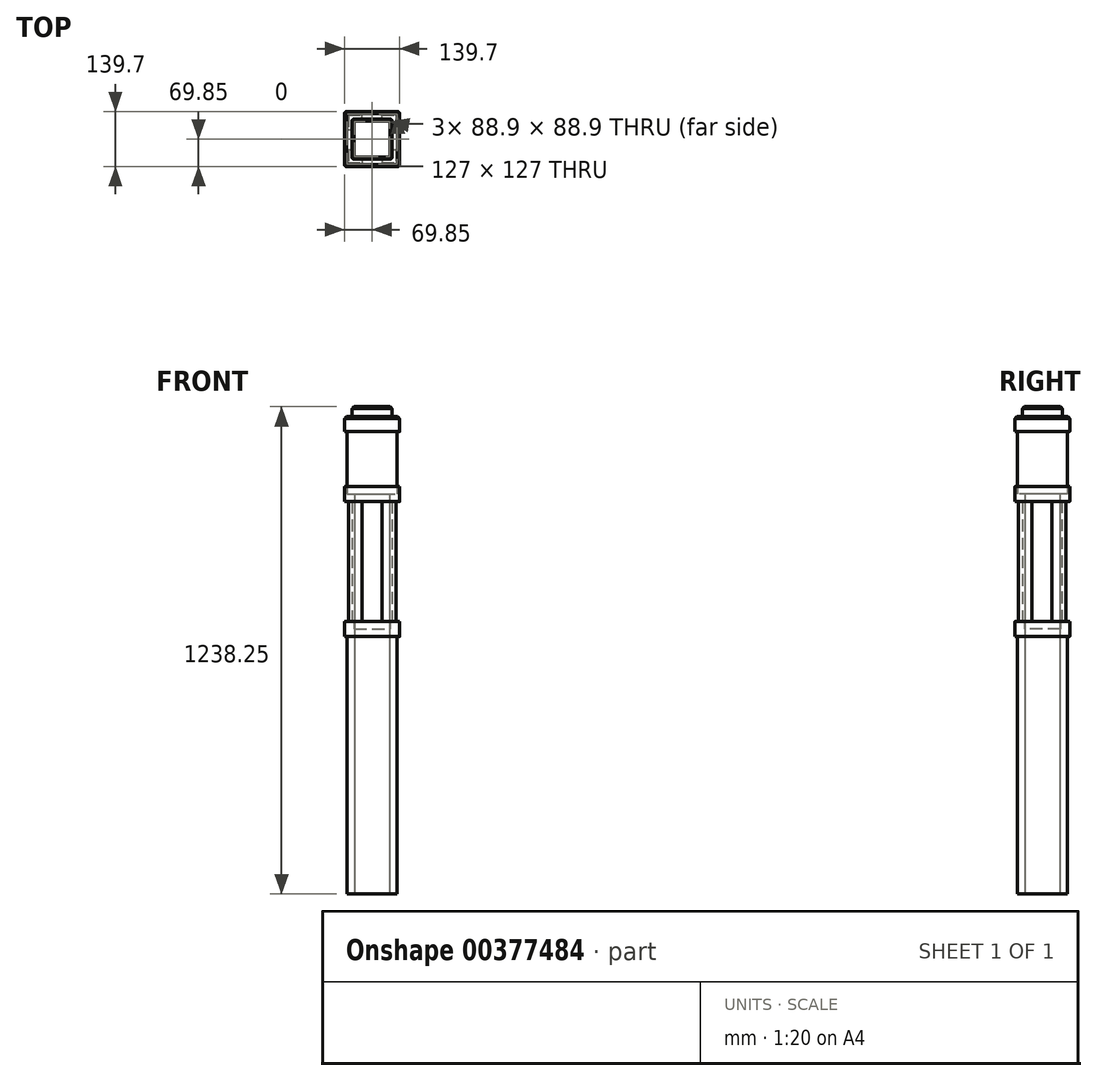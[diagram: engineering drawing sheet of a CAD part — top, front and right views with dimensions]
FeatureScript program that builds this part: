
annotation { "Feature Type Name" : "Feature", "Feature Type Description" : "" }
export const myFeature = defineFeature(function(context is Context, id is Id, definition is map)
    precondition{}
    {
        {
            var Q0;
            Q0=qCreatedBy(makeId("Top.planeOp"),FACE);
            var sketch = newSketch(context, id + "F0", { "sketchPlane" : qUnion([Q0])});
            skLineSegment(sketch, "E0.bottom", {"start": v(-44.45, 44.45) * mm, "end": v(44.45, 44.45) * mm});
            skLineSegment(sketch, "E0.top", {"start": v(-44.45, -44.45) * mm, "end": v(44.45, -44.45) * mm});
            skLineSegment(sketch, "E0.left", {"start": v(-44.45, 44.45) * mm, "end": v(-44.45, -44.45) * mm});
            skLineSegment(sketch, "E0.right", {"start": v(44.45, 44.45) * mm, "end": v(44.45, -44.45) * mm});
            skPoint(sketch, "E0.middle", {"position": v(0, 0) * mm});
            skSolve(sketch);
        }
        {
            var Q0;
            Q0 = qSketchRegion(id + "F0", true);
            extrude(context, id + "F1", {"entities" : qUnion([Q0]), "depth" : 1193.8 * mm, "offsetDistance" : 25.4 * mm});
        }
        {
            var Q0;
            Q0=makeQuery(id+"F1.opExtrude","CAP_FACE",FACE,{"disambiguationData":[OSD([sQuery(id+"F0.wireOp",EDGE,"E0.bottom"),sQuery(id+"F0.wireOp",EDGE,"E0.top"),sQuery(id+"F0.wireOp",EDGE,"E0.left"),sQuery(id+"F0.wireOp",EDGE,"E0.right")])],"isStart":true});
            var sketch = newSketch(context, id + "F2", { "sketchPlane" : qUnion([Q0])});
            skLineSegment(sketch, "E1.bottom", {"start": v(-63.5, 63.5) * mm, "end": v(63.5, 63.5) * mm});
            skLineSegment(sketch, "E1.top", {"start": v(-63.5, -63.5) * mm, "end": v(63.5, -63.5) * mm});
            skLineSegment(sketch, "E1.left", {"start": v(-63.5, 63.5) * mm, "end": v(-63.5, -63.5) * mm});
            skLineSegment(sketch, "E1.right", {"start": v(63.5, 63.5) * mm, "end": v(63.5, -63.5) * mm});
            skPoint(sketch, "E1.middle", {"position": v(0, 0) * mm});
            skLineSegment(sketch, "E2.bottom", {"start": v(-44.45, 44.45) * mm, "end": v(44.45, 44.45) * mm});
            skLineSegment(sketch, "E2.top", {"start": v(-44.45, -44.45) * mm, "end": v(44.45, -44.45) * mm});
            skLineSegment(sketch, "E2.left", {"start": v(-44.45, 44.45) * mm, "end": v(-44.45, -44.45) * mm});
            skLineSegment(sketch, "E2.right", {"start": v(44.45, 44.45) * mm, "end": v(44.45, -44.45) * mm});
            skLineSegment(sketch, "E3", {"start": v(44.45, 44.45) * mm, "end": v(63.5, 63.5) * mm});
            skLineSegment(sketch, "E4", {"start": v(44.45, -44.45) * mm, "end": v(63.5, -63.5) * mm});
            skLineSegment(sketch, "E5", {"start": v(-44.45, -44.45) * mm, "end": v(-63.5, -63.5) * mm});
            skLineSegment(sketch, "E6", {"start": v(-44.45, 44.45) * mm, "end": v(-63.5, 63.5) * mm});
            skSolve(sketch);
        }
        {
            var Q0;
            Q0 = qSketchRegion(id + "F2", true);
            extrude(context, id + "F3", {"entities" : qUnion([Q0]), "oppositeDirection" : true, "depth" : 673.1 * mm, "offsetDistance" : 25.4 * mm});
        }
        {
            var Q0;
            Q0=makeQuery(id+"F3.opExtrude","CAP_FACE",FACE,{"disambiguationData":[OSD([sQuery(id+"F2.wireOp",EDGE,"E1.bottom"),sQuery(id+"F2.wireOp",EDGE,"E1.top"),sQuery(id+"F2.wireOp",EDGE,"E1.left"),sQuery(id+"F2.wireOp",EDGE,"E1.right"),sQuery(id+"F2.wireOp",EDGE,"E2.bottom"),sQuery(id+"F2.wireOp",EDGE,"E2.top"),sQuery(id+"F2.wireOp",EDGE,"E2.left"),sQuery(id+"F2.wireOp",EDGE,"E2.right")])],"isStart":false});
            var sketch = newSketch(context, id + "F4", { "sketchPlane" : qUnion([Q0])});
            skLineSegment(sketch, "E7.bottom", {"start": v(-69.85, 69.85) * mm, "end": v(69.85, 69.85) * mm});
            skLineSegment(sketch, "E7.top", {"start": v(-69.85, -69.85) * mm, "end": v(69.85, -69.85) * mm});
            skLineSegment(sketch, "E7.left", {"start": v(-69.85, 69.85) * mm, "end": v(-69.85, -69.85) * mm});
            skLineSegment(sketch, "E7.right", {"start": v(69.85, 69.85) * mm, "end": v(69.85, -69.85) * mm});
            skPoint(sketch, "E7.middle", {"position": v(0, 0) * mm});
            skLineSegment(sketch, "E8.bottom", {"start": v(-63.5, 63.5) * mm, "end": v(63.5, 63.5) * mm});
            skLineSegment(sketch, "E8.top", {"start": v(-63.5, -63.5) * mm, "end": v(63.5, -63.5) * mm});
            skLineSegment(sketch, "E8.left", {"start": v(-63.5, 63.5) * mm, "end": v(-63.5, -63.5) * mm});
            skLineSegment(sketch, "E8.right", {"start": v(63.5, 63.5) * mm, "end": v(63.5, -63.5) * mm});
            skSolve(sketch);
        }
        {
            var Q0;
            Q0 = qSketchRegion(id + "F4", true);
            extrude(context, id + "F5", {"entities" : qUnion([Q0]), "oppositeDirection" : true, "depth" : 19.05 * mm, "offsetDistance" : 25.4 * mm});
        }
        {
            var Q0;
            Q0=makeQuery(id+"F5.opExtrude","CAP_FACE",FACE,{"disambiguationData":[OSD([sQuery(id+"F4.wireOp",EDGE,"E7.bottom"),sQuery(id+"F4.wireOp",EDGE,"E7.top"),sQuery(id+"F4.wireOp",EDGE,"E7.left"),sQuery(id+"F4.wireOp",EDGE,"E7.right"),sQuery(id+"F4.wireOp",EDGE,"E8.bottom"),sQuery(id+"F4.wireOp",EDGE,"E8.top"),sQuery(id+"F4.wireOp",EDGE,"E8.left"),sQuery(id+"F4.wireOp",EDGE,"E8.right")])],"isStart":true});
            var sketch = newSketch(context, id + "F6", { "sketchPlane" : qUnion([Q0])});
            skLineSegment(sketch, "E9.bottom", {"start": v(-69.85, 69.85) * mm, "end": v(69.85, 69.85) * mm});
            skLineSegment(sketch, "E9.top", {"start": v(-69.85, -69.85) * mm, "end": v(69.85, -69.85) * mm});
            skLineSegment(sketch, "E9.left", {"start": v(-69.85, 69.85) * mm, "end": v(-69.85, -69.85) * mm});
            skLineSegment(sketch, "E9.right", {"start": v(69.85, 69.85) * mm, "end": v(69.85, -69.85) * mm});
            skPoint(sketch, "E9.middle", {"position": v(0, 0) * mm});
            skLineSegment(sketch, "E10.bottom", {"start": v(-45.72, 45.72) * mm, "end": v(45.72, 45.72) * mm});
            skLineSegment(sketch, "E10.top", {"start": v(-45.72, -45.72) * mm, "end": v(45.72, -45.72) * mm});
            skLineSegment(sketch, "E10.left", {"start": v(-45.72, 45.72) * mm, "end": v(-45.72, -45.72) * mm});
            skLineSegment(sketch, "E10.right", {"start": v(45.72, 45.72) * mm, "end": v(45.72, -45.72) * mm});
            skSolve(sketch);
        }
        {
            var Q0;
            Q0 = qSketchRegion(id + "F6", true);
            extrude(context, id + "F7", {"entities" : qUnion([Q0]), "operationType" : NewBodyOperationType.ADD, "depth" : 19.05 * mm, "offsetDistance" : 25.4 * mm});
        }
        {
            var Q0;
            Q0=makeQuery(id+"F7.opExtrude","CAP_FACE",FACE,{"disambiguationData":[OSD([sQuery(id+"F6.wireOp",EDGE,"E9.bottom"),sQuery(id+"F6.wireOp",EDGE,"E9.top"),sQuery(id+"F6.wireOp",EDGE,"E9.left"),sQuery(id+"F6.wireOp",EDGE,"E9.right"),sQuery(id+"F6.wireOp",EDGE,"E10.bottom"),sQuery(id+"F6.wireOp",EDGE,"E10.top"),sQuery(id+"F6.wireOp",EDGE,"E10.left"),sQuery(id+"F6.wireOp",EDGE,"E10.right")])],"isStart":false});
            var sketch = newSketch(context, id + "F8", { "sketchPlane" : qUnion([Q0])});
            skLineSegment(sketch, "E11.bottom", {"start": v(-50.8, 50.8) * mm, "end": v(50.8, 50.8) * mm});
            skLineSegment(sketch, "E11.top", {"start": v(-50.8, -50.8) * mm, "end": v(50.8, -50.8) * mm});
            skLineSegment(sketch, "E11.left", {"start": v(-50.8, 50.8) * mm, "end": v(-50.8, -50.8) * mm});
            skLineSegment(sketch, "E11.right", {"start": v(50.8, 50.8) * mm, "end": v(50.8, -50.8) * mm});
            skPoint(sketch, "E11.middle", {"position": v(0, 0) * mm});
            skLineSegment(sketch, "E12.bottom", {"start": v(-44.45, 44.45) * mm, "end": v(44.45, 44.45) * mm});
            skLineSegment(sketch, "E12.top", {"start": v(-44.45, -44.45) * mm, "end": v(44.45, -44.45) * mm});
            skLineSegment(sketch, "E12.left", {"start": v(-44.45, 44.45) * mm, "end": v(-44.45, -44.45) * mm});
            skLineSegment(sketch, "E12.right", {"start": v(44.45, 44.45) * mm, "end": v(44.45, -44.45) * mm});
            skSolve(sketch);
        }
        {
            var Q0;
            Q0 = qSketchRegion(id + "F8", true);
            extrude(context, id + "F9", {"entities" : qUnion([Q0]), "depth" : 304.8 * mm, "offsetDistance" : 25.4 * mm});
        }
        {
            var Q0;
            Q0=makeQuery(id+"F9.opExtrude","CAP_FACE",FACE,{"disambiguationData":[OSD([sQuery(id+"F8.wireOp",EDGE,"E11.bottom"),sQuery(id+"F8.wireOp",EDGE,"E11.top"),sQuery(id+"F8.wireOp",EDGE,"E11.left"),sQuery(id+"F8.wireOp",EDGE,"E11.right"),sQuery(id+"F8.wireOp",EDGE,"E12.bottom"),sQuery(id+"F8.wireOp",EDGE,"E12.top"),sQuery(id+"F8.wireOp",EDGE,"E12.left"),sQuery(id+"F8.wireOp",EDGE,"E12.right")])],"isStart":false});
            var sketch = newSketch(context, id + "F10", { "sketchPlane" : qUnion([Q0])});
            skLineSegment(sketch, "E13.bottom", {"start": v(-69.85, 69.85) * mm, "end": v(69.85, 69.85) * mm});
            skLineSegment(sketch, "E13.top", {"start": v(-69.85, -69.85) * mm, "end": v(69.85, -69.85) * mm});
            skLineSegment(sketch, "E13.left", {"start": v(-69.85, 69.85) * mm, "end": v(-69.85, -69.85) * mm});
            skLineSegment(sketch, "E13.right", {"start": v(69.85, 69.85) * mm, "end": v(69.85, -69.85) * mm});
            skPoint(sketch, "E13.middle", {"position": v(0, 0) * mm});
            skLineSegment(sketch, "E14.bottom", {"start": v(-44.45, 44.45) * mm, "end": v(44.45, 44.45) * mm});
            skLineSegment(sketch, "E14.top", {"start": v(-44.45, -44.45) * mm, "end": v(44.45, -44.45) * mm});
            skLineSegment(sketch, "E14.left", {"start": v(-44.45, 44.45) * mm, "end": v(-44.45, -44.45) * mm});
            skLineSegment(sketch, "E14.right", {"start": v(44.45, 44.45) * mm, "end": v(44.45, -44.45) * mm});
            skSolve(sketch);
        }
        {
            var Q0;
            Q0 = qSketchRegion(id + "F10", true);
            extrude(context, id + "F11", {"entities" : qUnion([Q0]), "depth" : 19.05 * mm, "offsetDistance" : 25.4 * mm});
        }
        {
            var Q0;
            Q0=makeQuery(id+"F11.opExtrude","CAP_FACE",FACE,{"disambiguationData":[OSD([sQuery(id+"F10.wireOp",EDGE,"E13.bottom"),sQuery(id+"F10.wireOp",EDGE,"E13.top"),sQuery(id+"F10.wireOp",EDGE,"E13.left"),sQuery(id+"F10.wireOp",EDGE,"E13.right"),sQuery(id+"F10.wireOp",EDGE,"E14.bottom"),sQuery(id+"F10.wireOp",EDGE,"E14.top"),sQuery(id+"F10.wireOp",EDGE,"E14.left"),sQuery(id+"F10.wireOp",EDGE,"E14.right")])],"isStart":false});
            var sketch = newSketch(context, id + "F12", { "sketchPlane" : qUnion([Q0])});
            skLineSegment(sketch, "E15.bottom", {"start": v(-69.85, 69.85) * mm, "end": v(69.85, 69.85) * mm});
            skLineSegment(sketch, "E15.top", {"start": v(-69.85, -69.85) * mm, "end": v(69.85, -69.85) * mm});
            skLineSegment(sketch, "E15.left", {"start": v(-69.85, 69.85) * mm, "end": v(-69.85, -69.85) * mm});
            skLineSegment(sketch, "E15.right", {"start": v(69.85, 69.85) * mm, "end": v(69.85, -69.85) * mm});
            skPoint(sketch, "E15.middle", {"position": v(0, 0) * mm});
            skLineSegment(sketch, "E16.bottom", {"start": v(-63.5, 63.5) * mm, "end": v(63.5, 63.5) * mm});
            skLineSegment(sketch, "E16.top", {"start": v(-63.5, -63.5) * mm, "end": v(63.5, -63.5) * mm});
            skLineSegment(sketch, "E16.left", {"start": v(-63.5, 63.5) * mm, "end": v(-63.5, -63.5) * mm});
            skLineSegment(sketch, "E16.right", {"start": v(63.5, 63.5) * mm, "end": v(63.5, -63.5) * mm});
            skSolve(sketch);
        }
        {
            var Q0;
            Q0 = qSketchRegion(id + "F12", true);
            extrude(context, id + "F13", {"entities" : qUnion([Q0]), "operationType" : NewBodyOperationType.ADD, "depth" : 19.05 * mm, "offsetDistance" : 25.4 * mm});
        }
        {
            var Q0;
            Q0=makeQuery(id+"F11.opExtrude","CAP_FACE",FACE,{"disambiguationData":[OSD([sQuery(id+"F10.wireOp",EDGE,"E13.bottom"),sQuery(id+"F10.wireOp",EDGE,"E13.top"),sQuery(id+"F10.wireOp",EDGE,"E13.left"),sQuery(id+"F10.wireOp",EDGE,"E13.right"),sQuery(id+"F10.wireOp",EDGE,"E14.bottom"),sQuery(id+"F10.wireOp",EDGE,"E14.top"),sQuery(id+"F10.wireOp",EDGE,"E14.left"),sQuery(id+"F10.wireOp",EDGE,"E14.right")])],"isStart":false});
            var sketch = newSketch(context, id + "F14", { "sketchPlane" : qUnion([Q0])});
            skLineSegment(sketch, "E17.bottom", {"start": v(-63.5, 63.5) * mm, "end": v(63.5, 63.5) * mm});
            skLineSegment(sketch, "E17.top", {"start": v(-63.5, -63.5) * mm, "end": v(63.5, -63.5) * mm});
            skLineSegment(sketch, "E17.left", {"start": v(-63.5, 63.5) * mm, "end": v(-63.5, -63.5) * mm});
            skLineSegment(sketch, "E17.right", {"start": v(63.5, 63.5) * mm, "end": v(63.5, -63.5) * mm});
            skPoint(sketch, "E17.middle", {"position": v(0, 0) * mm});
            skLineSegment(sketch, "E18.bottom", {"start": v(-44.45, 44.45) * mm, "end": v(44.45, 44.45) * mm});
            skLineSegment(sketch, "E18.top", {"start": v(-44.45, -44.45) * mm, "end": v(44.45, -44.45) * mm});
            skLineSegment(sketch, "E18.left", {"start": v(-44.45, 44.45) * mm, "end": v(-44.45, -44.45) * mm});
            skLineSegment(sketch, "E18.right", {"start": v(44.45, 44.45) * mm, "end": v(44.45, -44.45) * mm});
            skSolve(sketch);
        }
        {
            var Q0;
            Q0 = qSketchRegion(id + "F14", true);
            extrude(context, id + "F15", {"entities" : qUnion([Q0]), "depth" : 177.8 * mm, "offsetDistance" : 25.4 * mm});
        }
        {
            var Q0;
            Q0=makeQuery(id+"F7.opExtrude","CAP_FACE",FACE,{"disambiguationData":[OSD([sQuery(id+"F6.wireOp",EDGE,"E9.bottom"),sQuery(id+"F6.wireOp",EDGE,"E9.top"),sQuery(id+"F6.wireOp",EDGE,"E9.left"),sQuery(id+"F6.wireOp",EDGE,"E9.right"),sQuery(id+"F6.wireOp",EDGE,"E10.bottom"),sQuery(id+"F6.wireOp",EDGE,"E10.top"),sQuery(id+"F6.wireOp",EDGE,"E10.left"),sQuery(id+"F6.wireOp",EDGE,"E10.right")])],"isStart":false});
            var sketch = newSketch(context, id + "F16", { "sketchPlane" : qUnion([Q0])});
            skLineSegment(sketch, "E19.bottom", {"start": v(-60.32, 60.33) * mm, "end": v(60.33, 60.33) * mm});
            skLineSegment(sketch, "E19.top", {"start": v(-60.33, -60.33) * mm, "end": v(60.32, -60.33) * mm});
            skLineSegment(sketch, "E19.left", {"start": v(-60.32, 60.33) * mm, "end": v(-60.33, -60.33) * mm});
            skLineSegment(sketch, "E19.right", {"start": v(60.33, 60.33) * mm, "end": v(60.32, -60.33) * mm});
            skPoint(sketch, "E19.middle", {"position": v(0, 0) * mm});
            skLineSegment(sketch, "E20.bottom", {"start": v(-50.8, -50.8) * mm, "end": v(50.8, -50.8) * mm});
            skLineSegment(sketch, "E20.top", {"start": v(-50.8, 50.8) * mm, "end": v(50.8, 50.8) * mm});
            skLineSegment(sketch, "E20.left", {"start": v(-50.8, -50.8) * mm, "end": v(-50.8, 50.8) * mm});
            skLineSegment(sketch, "E20.right", {"start": v(50.8, -50.8) * mm, "end": v(50.8, 50.8) * mm});
            skSolve(sketch);
        }
        {
            var Q0;
            Q0 = qSketchRegion(id + "F16", true);
            extrude(context, id + "F17", {"entities" : qUnion([Q0]), "depth" : 304.8 * mm, "offsetDistance" : 25.4 * mm});
        }
        {
            var Q0;
            Q0=makeQuery(id+"F17.opExtrude","CAP_FACE",FACE,{"disambiguationData":[OSD([sQuery(id+"F16.wireOp",EDGE,"E19.bottom"),sQuery(id+"F16.wireOp",EDGE,"E19.top"),sQuery(id+"F16.wireOp",EDGE,"E19.left"),sQuery(id+"F16.wireOp",EDGE,"E19.right"),sQuery(id+"F16.wireOp",EDGE,"E20.bottom"),sQuery(id+"F16.wireOp",EDGE,"E20.top"),sQuery(id+"F16.wireOp",EDGE,"E20.left"),sQuery(id+"F16.wireOp",EDGE,"E20.right")])],"isStart":false});
            var sketch = newSketch(context, id + "F18", { "sketchPlane" : qUnion([Q0])});
            skLineSegment(sketch, "E21.bottom", {"start": v(-60.32, 24.53) * mm, "end": v(-50.8, 24.53) * mm});
            skLineSegment(sketch, "E21.top", {"start": v(-60.32, -26.27) * mm, "end": v(-50.8, -26.27) * mm});
            skLineSegment(sketch, "E21.left", {"start": v(-60.32, 24.53) * mm, "end": v(-60.32, -26.27) * mm});
            skLineSegment(sketch, "E21.right", {"start": v(-50.8, 24.53) * mm, "end": v(-50.8, -26.27) * mm});
            skLineSegment(sketch, "E22.bottom", {"start": v(50.8, 24.53) * mm, "end": v(60.33, 24.53) * mm});
            skLineSegment(sketch, "E22.top", {"start": v(50.8, -26.27) * mm, "end": v(60.32, -26.27) * mm});
            skLineSegment(sketch, "E22.left", {"start": v(50.8, 24.53) * mm, "end": v(50.8, -26.27) * mm});
            skLineSegment(sketch, "E22.right", {"start": v(60.32, 24.53) * mm, "end": v(60.32, -26.27) * mm});
            skLineSegment(sketch, "E23.bottom", {"start": v(-25.4, 50.8) * mm, "end": v(25.4, 50.8) * mm});
            skLineSegment(sketch, "E23.top", {"start": v(-25.4, 60.33) * mm, "end": v(25.4, 60.33) * mm});
            skLineSegment(sketch, "E23.left", {"start": v(-25.4, 50.8) * mm, "end": v(-25.4, 60.33) * mm});
            skLineSegment(sketch, "E23.right", {"start": v(25.4, 50.8) * mm, "end": v(25.4, 60.33) * mm});
            skLineSegment(sketch, "E24.bottom", {"start": v(25.4, -50.8) * mm, "end": v(-25.4, -50.8) * mm});
            skLineSegment(sketch, "E24.top", {"start": v(25.4, -60.33) * mm, "end": v(-25.4, -60.33) * mm});
            skLineSegment(sketch, "E24.left", {"start": v(25.4, -50.8) * mm, "end": v(25.4, -60.33) * mm});
            skLineSegment(sketch, "E24.right", {"start": v(-25.4, -50.8) * mm, "end": v(-25.4, -60.33) * mm});
            skSolve(sketch);
        }
        {
            var Q0;
            Q0 = qSketchRegion(id + "F18", true);
            extrude(context, id + "F19", {"entities" : qUnion([Q0]), "operationType" : NewBodyOperationType.REMOVE, "oppositeDirection" : true, "depth" : 304.8 * mm, "offsetDistance" : 25.4 * mm});
        }
        {
            var Q0;
            Q0=makeQuery(id+"F1.opExtrude","CAP_FACE",FACE,{"disambiguationData":[OSD([sQuery(id+"F0.wireOp",EDGE,"E0.bottom"),sQuery(id+"F0.wireOp",EDGE,"E0.top"),sQuery(id+"F0.wireOp",EDGE,"E0.left"),sQuery(id+"F0.wireOp",EDGE,"E0.right")])],"isStart":false});
            var sketch = newSketch(context, id + "F20", { "sketchPlane" : qUnion([Q0])});
            skLineSegment(sketch, "E25.bottom", {"start": v(-69.85, 69.85) * mm, "end": v(69.85, 69.85) * mm});
            skLineSegment(sketch, "E25.top", {"start": v(-69.85, -69.85) * mm, "end": v(69.85, -69.85) * mm});
            skLineSegment(sketch, "E25.left", {"start": v(-69.85, 69.85) * mm, "end": v(-69.85, -69.85) * mm});
            skLineSegment(sketch, "E25.right", {"start": v(69.85, 69.85) * mm, "end": v(69.85, -69.85) * mm});
            skPoint(sketch, "E25.middle", {"position": v(0, 0) * mm});
            skLineSegment(sketch, "E26.bottom", {"start": v(-63.5, 63.5) * mm, "end": v(63.5, 63.5) * mm});
            skLineSegment(sketch, "E26.top", {"start": v(-63.5, -63.5) * mm, "end": v(63.5, -63.5) * mm});
            skLineSegment(sketch, "E26.left", {"start": v(-63.5, 63.5) * mm, "end": v(-63.5, -63.5) * mm});
            skLineSegment(sketch, "E26.right", {"start": v(63.5, 63.5) * mm, "end": v(63.5, -63.5) * mm});
            skSolve(sketch);
        }
        {
            var Q0;
            Q0 = qSketchRegion(id + "F20", true);
            extrude(context, id + "F21", {"entities" : qUnion([Q0]), "oppositeDirection" : true, "depth" : 19.05 * mm, "offsetDistance" : 25.4 * mm});
        }
        {
            var Q0;
            Q0=makeQuery(id+"F21.opExtrude","CAP_FACE",FACE,{"disambiguationData":[OSD([sQuery(id+"F20.wireOp",EDGE,"E25.bottom"),sQuery(id+"F20.wireOp",EDGE,"E25.top"),sQuery(id+"F20.wireOp",EDGE,"E25.left"),sQuery(id+"F20.wireOp",EDGE,"E25.right"),sQuery(id+"F20.wireOp",EDGE,"E26.bottom"),sQuery(id+"F20.wireOp",EDGE,"E26.top"),sQuery(id+"F20.wireOp",EDGE,"E26.left"),sQuery(id+"F20.wireOp",EDGE,"E26.right")])],"isStart":true});
            var sketch = newSketch(context, id + "F22", { "sketchPlane" : qUnion([Q0])});
            skLineSegment(sketch, "E27.bottom", {"start": v(-69.85, 69.85) * mm, "end": v(69.85, 69.85) * mm});
            skLineSegment(sketch, "E27.top", {"start": v(-69.85, -69.85) * mm, "end": v(69.85, -69.85) * mm});
            skLineSegment(sketch, "E27.left", {"start": v(-69.85, 69.85) * mm, "end": v(-69.85, -69.85) * mm});
            skLineSegment(sketch, "E27.right", {"start": v(69.85, 69.85) * mm, "end": v(69.85, -69.85) * mm});
            skPoint(sketch, "E27.middle", {"position": v(0, 0) * mm});
            skSolve(sketch);
        }
        {
            var Q0;
            Q0 = qSketchRegion(id + "F22", true);
            extrude(context, id + "F23", {"entities" : qUnion([Q0]), "operationType" : NewBodyOperationType.ADD, "depth" : 19.05 * mm, "offsetDistance" : 25.4 * mm});
        }
        {
            var Q0;
            Q0=makeQuery(id+"F23.opExtrude","CAP_FACE",FACE,{"disambiguationData":[OSD([sQuery(id+"F22.wireOp",EDGE,"E27.bottom"),sQuery(id+"F22.wireOp",EDGE,"E27.top"),sQuery(id+"F22.wireOp",EDGE,"E27.left"),sQuery(id+"F22.wireOp",EDGE,"E27.right")])],"isStart":false});
            var sketch = newSketch(context, id + "F24", { "sketchPlane" : qUnion([Q0])});
            skLineSegment(sketch, "E28.bottom", {"start": v(-50.8, 50.8) * mm, "end": v(50.8, 50.8) * mm});
            skLineSegment(sketch, "E28.top", {"start": v(-50.8, -50.8) * mm, "end": v(50.8, -50.8) * mm});
            skLineSegment(sketch, "E28.left", {"start": v(-50.8, 50.8) * mm, "end": v(-50.8, -50.8) * mm});
            skLineSegment(sketch, "E28.right", {"start": v(50.8, 50.8) * mm, "end": v(50.8, -50.8) * mm});
            skPoint(sketch, "E28.middle", {"position": v(0, 0) * mm});
            skSolve(sketch);
        }
        {
            var Q0;
            Q0 = qSketchRegion(id + "F24", true);
            extrude(context, id + "F25", {"entities" : qUnion([Q0]), "operationType" : NewBodyOperationType.ADD, "depth" : 25.4 * mm, "offsetDistance" : 25.4 * mm});
        }
        {
            var Q0;
            Q0=makeQuery(id+"F25.opExtrude","CAP_FACE",FACE,{"disambiguationData":[OSD([sQuery(id+"F24.wireOp",EDGE,"E28.bottom"),sQuery(id+"F24.wireOp",EDGE,"E28.top"),sQuery(id+"F24.wireOp",EDGE,"E28.left"),sQuery(id+"F24.wireOp",EDGE,"E28.right")])],"isStart":false});
            var Q1;
            Q1=makeQuery(id+"F23.opExtrude","CAP_EDGE",EDGE,{"disambiguationData":[OSD([sQuery(id+"F22.wireOp",EDGE,"E27.right")])],"isStart":false});
            var Q2;
            Q2=makeQuery(id+"F23.opExtrude","CAP_EDGE",EDGE,{"disambiguationData":[OSD([sQuery(id+"F22.wireOp",EDGE,"E27.top")])],"isStart":false});
            var Q3;
            Q3=makeQuery(id+"F23.opExtrude","CAP_EDGE",EDGE,{"disambiguationData":[OSD([sQuery(id+"F22.wireOp",EDGE,"E27.left")])],"isStart":false});
            var Q4;
            Q4=makeQuery(id+"F23.opExtrude","CAP_EDGE",EDGE,{"disambiguationData":[OSD([sQuery(id+"F22.wireOp",EDGE,"E27.bottom")])],"isStart":false});
            chamfer(context, id + "F26", {"entities" : qUnion([Q0, Q1, Q2, Q3, Q4]), "width" : 5.08 * mm, "tangentPropagation" : true});
        }
        {
            var Q0;
            Q0=makeQuery(id+"F13.boolean.opBoolean","MERGE",EDGE,{"derivedFrom":[makeQuery(id+"F11.opExtrude","SWEPT_EDGE",EDGE,{"disambiguationData":[OSD([sQuery(id+"F10.wireOp",EDGE,"E13.top"),sQuery(id+"F10.wireOp",EDGE,"E13.left")])]}),makeQuery(id+"F13.opExtrude","SWEPT_EDGE",EDGE,{"disambiguationData":[OSD([sQuery(id+"F12.wireOp",EDGE,"E15.top"),sQuery(id+"F12.wireOp",EDGE,"E15.left")])]})]});
            var Q1;
            Q1=makeQuery(id+"F13.boolean.opBoolean","MERGE",EDGE,{"derivedFrom":[makeQuery(id+"F11.opExtrude","SWEPT_EDGE",EDGE,{"disambiguationData":[OSD([sQuery(id+"F10.wireOp",EDGE,"E13.top"),sQuery(id+"F10.wireOp",EDGE,"E13.right")])]}),makeQuery(id+"F13.opExtrude","SWEPT_EDGE",EDGE,{"disambiguationData":[OSD([sQuery(id+"F12.wireOp",EDGE,"E15.top"),sQuery(id+"F12.wireOp",EDGE,"E15.right")])]})]});
            var Q2;
            Q2=makeQuery(id+"F13.boolean.opBoolean","MERGE",EDGE,{"derivedFrom":[makeQuery(id+"F11.opExtrude","SWEPT_EDGE",EDGE,{"disambiguationData":[OSD([sQuery(id+"F10.wireOp",EDGE,"E13.bottom"),sQuery(id+"F10.wireOp",EDGE,"E13.left")])]}),makeQuery(id+"F13.opExtrude","SWEPT_EDGE",EDGE,{"disambiguationData":[OSD([sQuery(id+"F12.wireOp",EDGE,"E15.bottom"),sQuery(id+"F12.wireOp",EDGE,"E15.left")])]})]});
            var Q3;
            Q3=makeQuery(id+"F13.boolean.opBoolean","MERGE",EDGE,{"derivedFrom":[makeQuery(id+"F11.opExtrude","SWEPT_EDGE",EDGE,{"disambiguationData":[OSD([sQuery(id+"F10.wireOp",EDGE,"E13.bottom"),sQuery(id+"F10.wireOp",EDGE,"E13.right")])]}),makeQuery(id+"F13.opExtrude","SWEPT_EDGE",EDGE,{"disambiguationData":[OSD([sQuery(id+"F12.wireOp",EDGE,"E15.bottom"),sQuery(id+"F12.wireOp",EDGE,"E15.right")])]})]});
            var Q4;
            Q4=makeQuery(id+"F23.boolean.opBoolean","MERGE",EDGE,{"derivedFrom":[makeQuery(id+"F21.opExtrude","SWEPT_EDGE",EDGE,{"disambiguationData":[OSD([sQuery(id+"F20.wireOp",EDGE,"E25.bottom"),sQuery(id+"F20.wireOp",EDGE,"E25.right")])]}),makeQuery(id+"F23.opExtrude","SWEPT_EDGE",EDGE,{"disambiguationData":[OSD([sQuery(id+"F22.wireOp",EDGE,"E27.bottom"),sQuery(id+"F22.wireOp",EDGE,"E27.right")])]})]});
            var Q5;
            Q5=makeQuery(id+"F25.opExtrude","SWEPT_EDGE",EDGE,{"disambiguationData":[OSD([sQuery(id+"F24.wireOp",EDGE,"E28.bottom"),sQuery(id+"F24.wireOp",EDGE,"E28.right")])]});
            var Q6;
            Q6=makeQuery(id+"F7.boolean.opBoolean","MERGE",EDGE,{"derivedFrom":[makeQuery(id+"F5.opExtrude","SWEPT_EDGE",EDGE,{"disambiguationData":[OSD([sQuery(id+"F4.wireOp",EDGE,"E7.bottom"),sQuery(id+"F4.wireOp",EDGE,"E7.right")])]}),makeQuery(id+"F7.opExtrude","SWEPT_EDGE",EDGE,{"disambiguationData":[OSD([sQuery(id+"F6.wireOp",EDGE,"E9.bottom"),sQuery(id+"F6.wireOp",EDGE,"E9.right")])]})]});
            var Q7;
            Q7=makeQuery(id+"F7.boolean.opBoolean","MERGE",EDGE,{"derivedFrom":[makeQuery(id+"F5.opExtrude","SWEPT_EDGE",EDGE,{"disambiguationData":[OSD([sQuery(id+"F4.wireOp",EDGE,"E7.top"),sQuery(id+"F4.wireOp",EDGE,"E7.right")])]}),makeQuery(id+"F7.opExtrude","SWEPT_EDGE",EDGE,{"disambiguationData":[OSD([sQuery(id+"F6.wireOp",EDGE,"E9.top"),sQuery(id+"F6.wireOp",EDGE,"E9.right")])]})]});
            var Q8;
            Q8=makeQuery(id+"F23.boolean.opBoolean","MERGE",EDGE,{"derivedFrom":[makeQuery(id+"F21.opExtrude","SWEPT_EDGE",EDGE,{"disambiguationData":[OSD([sQuery(id+"F20.wireOp",EDGE,"E25.top"),sQuery(id+"F20.wireOp",EDGE,"E25.right")])]}),makeQuery(id+"F23.opExtrude","SWEPT_EDGE",EDGE,{"disambiguationData":[OSD([sQuery(id+"F22.wireOp",EDGE,"E27.top"),sQuery(id+"F22.wireOp",EDGE,"E27.right")])]})]});
            var Q9;
            Q9=makeQuery(id+"F25.opExtrude","SWEPT_EDGE",EDGE,{"disambiguationData":[OSD([sQuery(id+"F24.wireOp",EDGE,"E28.top"),sQuery(id+"F24.wireOp",EDGE,"E28.right")])]});
            var Q10;
            Q10=makeQuery(id+"F7.boolean.opBoolean","MERGE",EDGE,{"derivedFrom":[makeQuery(id+"F5.opExtrude","SWEPT_EDGE",EDGE,{"disambiguationData":[OSD([sQuery(id+"F4.wireOp",EDGE,"E7.top"),sQuery(id+"F4.wireOp",EDGE,"E7.left")])]}),makeQuery(id+"F7.opExtrude","SWEPT_EDGE",EDGE,{"disambiguationData":[OSD([sQuery(id+"F6.wireOp",EDGE,"E9.top"),sQuery(id+"F6.wireOp",EDGE,"E9.left")])]})]});
            var Q11;
            Q11=makeQuery(id+"F23.boolean.opBoolean","MERGE",EDGE,{"derivedFrom":[makeQuery(id+"F21.opExtrude","SWEPT_EDGE",EDGE,{"disambiguationData":[OSD([sQuery(id+"F20.wireOp",EDGE,"E25.top"),sQuery(id+"F20.wireOp",EDGE,"E25.left")])]}),makeQuery(id+"F23.opExtrude","SWEPT_EDGE",EDGE,{"disambiguationData":[OSD([sQuery(id+"F22.wireOp",EDGE,"E27.top"),sQuery(id+"F22.wireOp",EDGE,"E27.left")])]})]});
            var Q12;
            Q12=makeQuery(id+"F25.opExtrude","SWEPT_EDGE",EDGE,{"disambiguationData":[OSD([sQuery(id+"F24.wireOp",EDGE,"E28.top"),sQuery(id+"F24.wireOp",EDGE,"E28.left")])]});
            var Q13;
            Q13=makeQuery(id+"F7.boolean.opBoolean","MERGE",EDGE,{"derivedFrom":[makeQuery(id+"F5.opExtrude","SWEPT_EDGE",EDGE,{"disambiguationData":[OSD([sQuery(id+"F4.wireOp",EDGE,"E7.bottom"),sQuery(id+"F4.wireOp",EDGE,"E7.left")])]}),makeQuery(id+"F7.opExtrude","SWEPT_EDGE",EDGE,{"disambiguationData":[OSD([sQuery(id+"F6.wireOp",EDGE,"E9.bottom"),sQuery(id+"F6.wireOp",EDGE,"E9.left")])]})]});
            var Q14;
            Q14=makeQuery(id+"F23.boolean.opBoolean","MERGE",EDGE,{"derivedFrom":[makeQuery(id+"F21.opExtrude","SWEPT_EDGE",EDGE,{"disambiguationData":[OSD([sQuery(id+"F20.wireOp",EDGE,"E25.bottom"),sQuery(id+"F20.wireOp",EDGE,"E25.left")])]}),makeQuery(id+"F23.opExtrude","SWEPT_EDGE",EDGE,{"disambiguationData":[OSD([sQuery(id+"F22.wireOp",EDGE,"E27.bottom"),sQuery(id+"F22.wireOp",EDGE,"E27.left")])]})]});
            var Q15;
            Q15=makeQuery(id+"F25.opExtrude","SWEPT_EDGE",EDGE,{"disambiguationData":[OSD([sQuery(id+"F24.wireOp",EDGE,"E28.bottom"),sQuery(id+"F24.wireOp",EDGE,"E28.left")])]});
            fillet(context, id + "F27", {"entities" : qUnion([Q0, Q1, Q2, Q3, Q4, Q5, Q6, Q7, Q8, Q9, Q10, Q11, Q12, Q13, Q14, Q15]), "tangentPropagation" : true, "radius" : 5.08 * mm, "defaultsChanged" : false, "vertexSettings" : [], "allowEdgeOverflow" : false});
        }
    });
